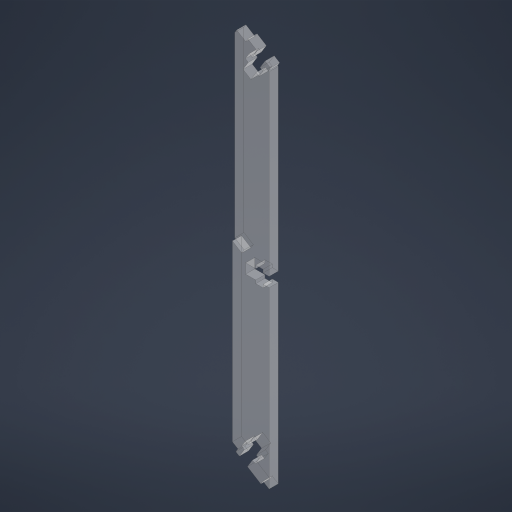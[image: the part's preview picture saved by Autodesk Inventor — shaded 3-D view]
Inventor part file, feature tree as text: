
AUTODESK INVENTOR PART (.ipt)
format: ipt  version: 2023 (Build 270158000, 158)  size: 304,128 bytes
history: native  units: in
note: dims shown in document units (in); Inventor stores cm internally (conversion verified against a paired STEP export)
features: reference x14, other x7, plane x1, extrude x1, sketch x1
ambient origin geometry x8: Origin, YZ Plane, XZ Plane, XY Plane, X Axis, Y Axis, Z Axis, Center Point
bodies: Solid1 (feature_tree)
feature tree (24):
  plane  "Work Plane1"
  extrude  "Extrusion1"  Depth=0.125in
  sketch  "Sketch1"  dims[d0=0.125in d1=0.125in d2=0.0796in d3=0.0796in d5=0.75in d7=0.015in d8=0.015in d10=0.35in d11=0.4375in d12=0.2in d13=0.4375in d14=0.2in d15=0.75in d16=0.4375in d17=0.2in d18=0.3in d19=0.25in d20=0.0in d21=0.015in d22=0.75in]
  reference  "Reference1"
  reference  "Reference3"
  reference  "Reference4"
  reference  "Reference5"
  reference  "Reference8"
  reference  "Reference9"
  reference  "Reference12"
  reference  "Reference13"
  reference  "Reference14"
  reference  "Reference17"
  reference  "Reference18"
  reference  "Reference19"
  reference  "Reference20"
  reference  "Reference21"
  other  "<userpath>\Desktop\WaccaController\Wacca Controller\Touch Segment\Touch Segment.iam"
  other  "Touch Segment.iam"
  other  "Front Plate:1"
  other  "Back Plate:1"
  other  "Touch Fifth:3"
  other  "Center Plate:1"
  other  "<userpath>\Desktop\Wacca Controller V3\Touch Segment\Touch Segment.iam"
